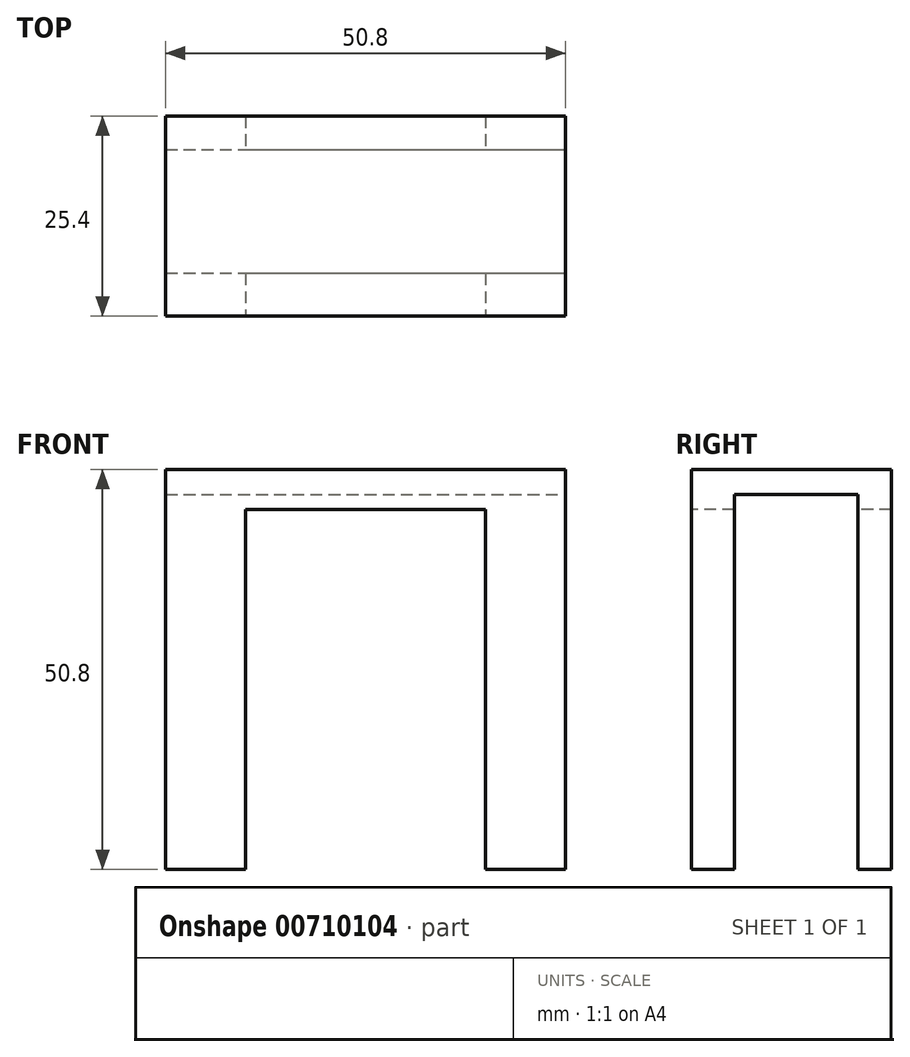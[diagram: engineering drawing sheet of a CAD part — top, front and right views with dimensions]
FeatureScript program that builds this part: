
annotation { "Feature Type Name" : "Feature", "Feature Type Description" : "" }
export const myFeature = defineFeature(function(context is Context, id is Id, definition is map)
    precondition{}
    {
        {
            var Q0;
            Q0=qCreatedBy(makeId("Front.planeOp"),FACE);
            var sketch = newSketch(context, id + "F0", { "sketchPlane" : qUnion([Q0])});
            skLineSegment(sketch, "E0.bottom", {"start": v(-25.4, 25.4) * mm, "end": v(25.4, 25.4) * mm});
            skLineSegment(sketch, "E0.top", {"start": v(-25.4, -25.4) * mm, "end": v(25.4, -25.4) * mm});
            skLineSegment(sketch, "E0.left", {"start": v(-25.4, 25.4) * mm, "end": v(-25.4, -25.4) * mm});
            skLineSegment(sketch, "E0.right", {"start": v(25.4, 25.4) * mm, "end": v(25.4, -25.4) * mm});
            skPoint(sketch, "E0.middle", {"position": v(0, 0) * mm});
            skSolve(sketch);
        }
        {
            var Q0;
            Q0 = qSketchRegion(id + "F0", true);
            extrude(context, id + "F1", {"entities" : qUnion([Q0]), "depth" : 25.4 * mm, "offsetDistance" : 25.4 * mm});
        }
        {
            var Q0;
            Q0=makeQuery(id+"F1.opExtrude","CAP_FACE",FACE,{"disambiguationData":[OSD([sQuery(id+"F0.wireOp",EDGE,"E0.bottom"),sQuery(id+"F0.wireOp",EDGE,"E0.top"),sQuery(id+"F0.wireOp",EDGE,"E0.left"),sQuery(id+"F0.wireOp",EDGE,"E0.right")])],"isStart":false});
            var sketch = newSketch(context, id + "F2", { "sketchPlane" : qUnion([Q0])});
            skLineSegment(sketch, "E1.bottom", {"start": v(-15.24, -25.4) * mm, "end": v(15.24, -25.4) * mm});
            skLineSegment(sketch, "E1.top", {"start": v(-15.24, 20.32) * mm, "end": v(15.24, 20.32) * mm});
            skLineSegment(sketch, "E1.left", {"start": v(-15.24, -25.4) * mm, "end": v(-15.24, 20.32) * mm});
            skLineSegment(sketch, "E1.right", {"start": v(15.24, -25.4) * mm, "end": v(15.24, 20.32) * mm});
            skSolve(sketch);
        }
        {
            var Q0;
            Q0=makeQuery(id+"F2.imprint","IMPRINT",FACE,{"disambiguationData":[TD([[makeQuery(id+"F2.imprint","IMPRINT",EDGE,{"derivedFrom":sQuery(id+"F2.wireOp",EDGE,"E1.bottom")}),1.0]])]});
            extrude(context, id + "F3", {"entities" : qUnion([Q0]), "operationType" : NewBodyOperationType.REMOVE, "endBound" : BoundingType.THROUGH_ALL, "oppositeDirection" : true, "depth" : 25.4 * mm, "offsetDistance" : 25.4 * mm});
        }
        {
            var Q0;
            Q0=makeQuery(id+"F1.opExtrude","SWEPT_FACE",FACE,{"disambiguationData":[OSD([sQuery(id+"F0.wireOp",EDGE,"E0.right")])]});
            var sketch = newSketch(context, id + "F4", { "sketchPlane" : qUnion([Q0])});
            skLineSegment(sketch, "E2.bottom", {"start": v(-19.97, -25.4) * mm, "end": v(-4.23, -25.4) * mm});
            skLineSegment(sketch, "E2.top", {"start": v(-19.97, 22.2) * mm, "end": v(-4.23, 22.2) * mm});
            skLineSegment(sketch, "E2.left", {"start": v(-19.97, -25.4) * mm, "end": v(-19.97, 22.2) * mm});
            skLineSegment(sketch, "E2.right", {"start": v(-4.23, -25.4) * mm, "end": v(-4.23, 22.2) * mm});
            skSolve(sketch);
        }
        {
            var Q0;
            Q0 = qSketchRegion(id + "F4", true);
            extrude(context, id + "F5", {"entities" : qUnion([Q0]), "operationType" : NewBodyOperationType.REMOVE, "endBound" : BoundingType.THROUGH_ALL, "oppositeDirection" : true, "depth" : 25.4 * mm, "offsetDistance" : 25.4 * mm});
        }
    });
